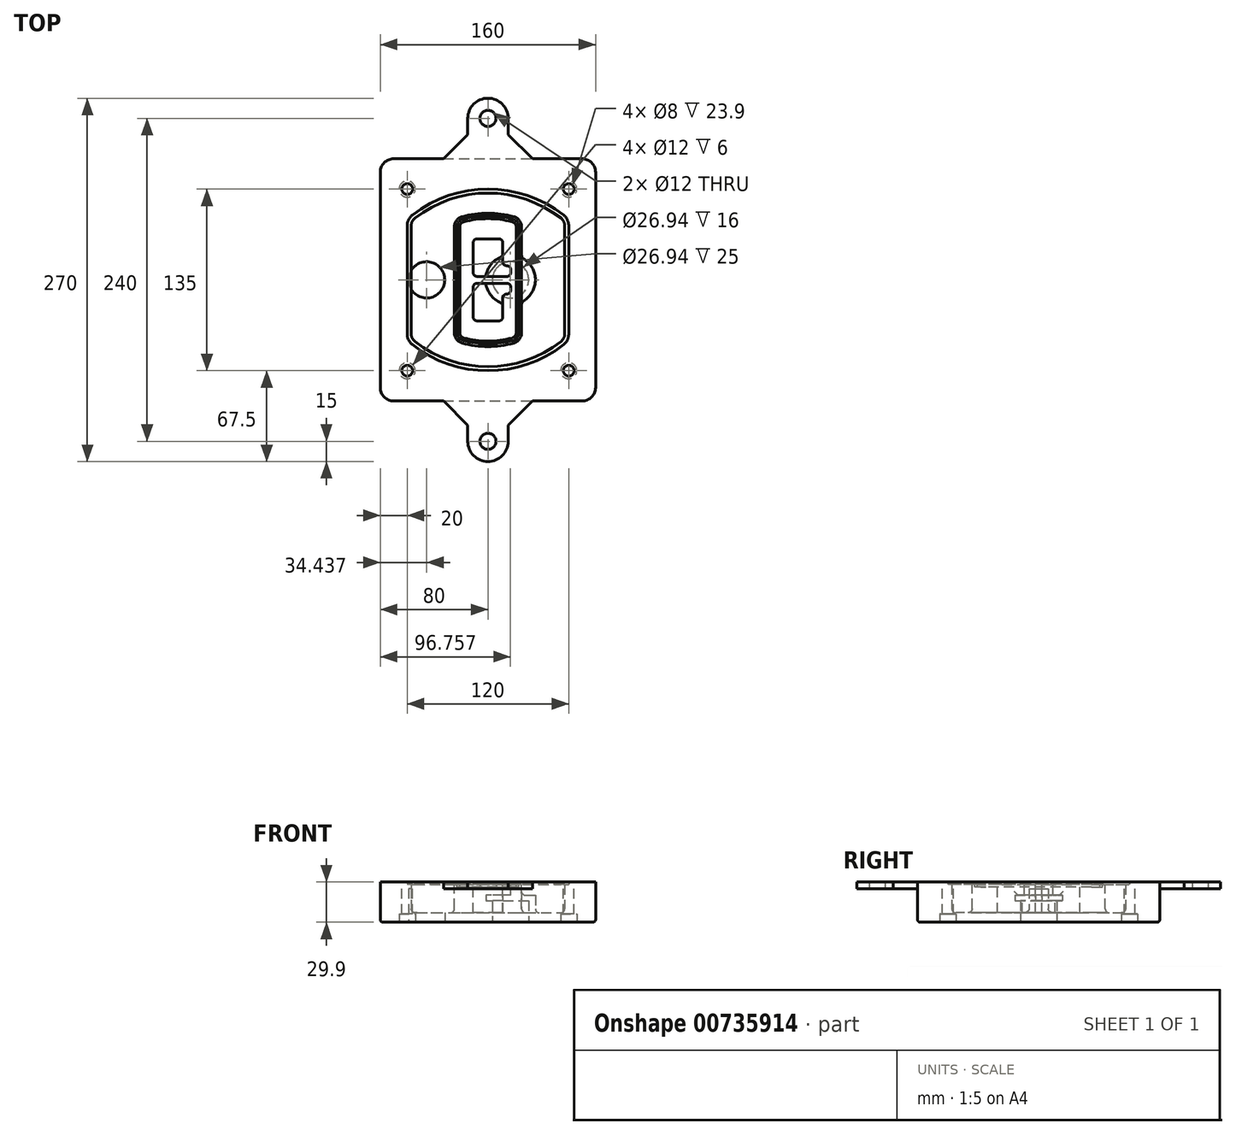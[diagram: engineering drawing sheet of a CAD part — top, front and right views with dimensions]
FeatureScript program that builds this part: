
annotation { "Feature Type Name" : "Feature", "Feature Type Description" : "" }
export const myFeature = defineFeature(function(context is Context, id is Id, definition is map)
    precondition{}
    {
        {
            var Q0;
            Q0=qCreatedBy(makeId("Top.planeOp"),FACE);
            var sketch = newSketch(context, id + "F0", { "sketchPlane" : qUnion([Q0])});
            skPoint(sketch, "E0.rect.middle", {"position": v(0, 0) * mm});
            skLineSegment(sketch, "E1.bottom", {"start": v(-70, -90) * mm, "end": v(70, -90) * mm});
            skLineSegment(sketch, "E1.top", {"start": v(-70, 90) * mm, "end": v(70, 90) * mm});
            skLineSegment(sketch, "E1.left", {"start": v(-80, -80) * mm, "end": v(-80, 80) * mm});
            skLineSegment(sketch, "E1.right", {"start": v(80, -80) * mm, "end": v(80, 80) * mm});
            skLineSegment(sketch, "E2", {"start": v(-80, 90) * mm, "end": v(80, -90) * mm, "construction": true});
            skLineSegment(sketch, "E3", {"start": v(80, 90) * mm, "end": v(-80, -90) * mm, "construction": true});
            skCircle(sketch, "E4", {"center": v(-60, 67.5) * mm, "radius": 4 * mm});
            skCircle(sketch, "E5", {"center": v(60, 67.5) * mm, "radius": 4 * mm});
            skCircle(sketch, "E6", {"center": v(60, -67.5) * mm, "radius": 4 * mm});
            skCircle(sketch, "E7", {"center": v(-60, -67.5) * mm, "radius": 4 * mm});
            skLineSegment(sketch, "E8", {"start": v(-60, 67.5) * mm, "end": v(60, 67.5) * mm, "construction": true});
            skLineSegment(sketch, "E9", {"start": v(60, 67.5) * mm, "end": v(60, -67.5) * mm, "construction": true});
            skLineSegment(sketch, "E10", {"start": v(60, -67.5) * mm, "end": v(-60, -67.5) * mm, "construction": true});
            skLineSegment(sketch, "E11", {"start": v(-60, -67.5) * mm, "end": v(-60, 67.5) * mm, "construction": true});
            skLineSegment(sketch, "E12", {"start": v(-60, 40.3) * mm, "end": v(-60, -40.3) * mm});
            skLineSegment(sketch, "E13", {"start": v(60, 40.3) * mm, "end": v(60, -40.3) * mm});
            skArc(sketch, "E14", {"start": v(56.15, 48.18) * mm, "mid": v(0, 67.5) * mm, "end": v(-56.15, 48.18) * mm});
            skArc(sketch, "E15", {"start": v(-56.15, -48.18) * mm, "mid": v(0, -67.5) * mm, "end": v(56.15, -48.18) * mm});
            skLineSegment(sketch, "E16", {"start": v(-60, 0) * mm, "end": v(60, 0) * mm, "construction": true});
            skPoint(sketch, "E17.visualSharp", {"position": v(-60, -45) * mm});
            skArc(sketch, "E17.filletArc", {"start": v(-60, -40.3) * mm, "mid": v(-58.99, -44.68) * mm, "end": v(-56.15, -48.18) * mm});
            skPoint(sketch, "E18.visualSharp", {"position": v(-60, 45) * mm});
            skArc(sketch, "E18.filletArc", {"start": v(-56.15, 48.18) * mm, "mid": v(-58.99, 44.68) * mm, "end": v(-60, 40.3) * mm});
            skPoint(sketch, "E19.visualSharp", {"position": v(60, 45) * mm});
            skArc(sketch, "E19.filletArc", {"start": v(60, 40.3) * mm, "mid": v(58.99, 44.68) * mm, "end": v(56.15, 48.18) * mm});
            skPoint(sketch, "E20.visualSharp", {"position": v(60, -45) * mm});
            skArc(sketch, "E20.filletArc", {"start": v(56.15, -48.18) * mm, "mid": v(58.99, -44.68) * mm, "end": v(60, -40.3) * mm});
            skPoint(sketch, "E21.visualSharp", {"position": v(-80, 90) * mm});
            skArc(sketch, "E21.filletArc", {"start": v(-70, 90) * mm, "mid": v(-77.07, 87.07) * mm, "end": v(-80, 80) * mm});
            skPoint(sketch, "E22.visualSharp", {"position": v(80, 90) * mm});
            skArc(sketch, "E22.filletArc", {"start": v(80, 80) * mm, "mid": v(77.07, 87.07) * mm, "end": v(70, 90) * mm});
            skPoint(sketch, "E23.visualSharp", {"position": v(80, -90) * mm});
            skArc(sketch, "E23.filletArc", {"start": v(70, -90) * mm, "mid": v(77.07, -87.07) * mm, "end": v(80, -80) * mm});
            skPoint(sketch, "E24.visualSharp", {"position": v(-80, -90) * mm});
            skArc(sketch, "E24.filletArc", {"start": v(-80, -80) * mm, "mid": v(-77.07, -87.07) * mm, "end": v(-70, -90) * mm});
            skArc(sketch, "E25.0", {"start": v(57, 40.3) * mm, "mid": v(56.3, 43.36) * mm, "end": v(54.3, 45.81) * mm});
            skLineSegment(sketch, "E25.1", {"start": v(57, 40.3) * mm, "end": v(57, -40.3) * mm});
            skArc(sketch, "E25.2", {"start": v(54.3, -45.81) * mm, "mid": v(56.3, -43.36) * mm, "end": v(57, -40.3) * mm});
            skArc(sketch, "E25.3", {"start": v(-54.3, -45.81) * mm, "mid": v(0, -64.5) * mm, "end": v(54.3, -45.81) * mm});
            skArc(sketch, "E25.4", {"start": v(-57, -40.3) * mm, "mid": v(-56.3, -43.36) * mm, "end": v(-54.3, -45.81) * mm});
            skArc(sketch, "E25.5", {"start": v(54.3, 45.81) * mm, "mid": v(0, 64.5) * mm, "end": v(-54.3, 45.81) * mm});
            skLineSegment(sketch, "E25.6", {"start": v(-57, 40.3) * mm, "end": v(-57, -40.3) * mm});
            skArc(sketch, "E25.7", {"start": v(-54.3, 45.81) * mm, "mid": v(-56.3, 43.36) * mm, "end": v(-57, 40.3) * mm});
            skArc(sketch, "E26.0", {"start": v(-58.62, 51.33) * mm, "mid": v(-62.58, 46.43) * mm, "end": v(-64, 40.3) * mm});
            skArc(sketch, "E26.1", {"start": v(58.62, 51.33) * mm, "mid": v(0, 71.5) * mm, "end": v(-58.62, 51.33) * mm});
            skArc(sketch, "E26.2", {"start": v(64, 40.3) * mm, "mid": v(62.58, 46.43) * mm, "end": v(58.62, 51.33) * mm});
            skLineSegment(sketch, "E26.3", {"start": v(64, 40.3) * mm, "end": v(64, -40.3) * mm});
            skArc(sketch, "E26.4", {"start": v(58.62, -51.33) * mm, "mid": v(62.58, -46.43) * mm, "end": v(64, -40.3) * mm});
            skLineSegment(sketch, "E26.5", {"start": v(-64, 40.3) * mm, "end": v(-64, -40.3) * mm});
            skArc(sketch, "E26.6", {"start": v(-58.62, -51.33) * mm, "mid": v(0, -71.5) * mm, "end": v(58.62, -51.33) * mm});
            skArc(sketch, "E26.7", {"start": v(-64, -40.3) * mm, "mid": v(-62.58, -46.43) * mm, "end": v(-58.62, -51.33) * mm});
            skSolve(sketch);
        }
        {
            var Q0;
            Q0=makeQuery(id+"F0.imprint","IMPRINT",FACE,{"disambiguationData":[TD([[makeQuery(id+"F0.imprint","IMPRINT",EDGE,{"derivedFrom":sQuery(id+"F0.wireOp",EDGE,"E1.bottom")}),1.0]])]});
            var Q1;
            Q1=makeQuery(id+"F0.imprint","IMPRINT",FACE,{"disambiguationData":[TD([[makeQuery(id+"F0.imprint","IMPRINT",EDGE,{"derivedFrom":sQuery(id+"F0.wireOp",EDGE,"E12")}),1.0]])]});
            var Q2;
            Q2=makeQuery(id+"F0.imprint","IMPRINT",FACE,{"disambiguationData":[TD([[makeQuery(id+"F0.imprint","IMPRINT",EDGE,{"derivedFrom":sQuery(id+"F0.wireOp",EDGE,"E25.0")}),1.0]])]});
            var Q3;
            Q3=makeQuery(id+"F0.imprint","IMPRINT",FACE,{"disambiguationData":[TD([[makeQuery(id+"F0.imprint","IMPRINT",EDGE,{"derivedFrom":sQuery(id+"F0.wireOp",EDGE,"E12")}),-1.0]])]});
            extrude(context, id + "F1", {"entities" : qUnion([Q0, Q1, Q2, Q3]), "oppositeDirection" : true, "depth" : 25 * mm});
        }
        {
            var Q0;
            Q0=makeQuery(id+"F0.imprint","IMPRINT",FACE,{"disambiguationData":[TD([[makeQuery(id+"F0.imprint","IMPRINT",EDGE,{"derivedFrom":sQuery(id+"F0.wireOp",EDGE,"E12")}),1.0]])]});
            extrude(context, id + "F2", {"entities" : qUnion([Q0]), "operationType" : NewBodyOperationType.ADD, "depth" : 3 * mm});
        }
        {
            var Q0;
            Q0=makeQuery(id+"F0.imprint","IMPRINT",FACE,{"disambiguationData":[TD([[makeQuery(id+"F0.imprint","IMPRINT",EDGE,{"derivedFrom":sQuery(id+"F0.wireOp",EDGE,"E25.0")}),1.0]])]});
            extrude(context, id + "F3", {"entities" : qUnion([Q0]), "operationType" : NewBodyOperationType.REMOVE, "oppositeDirection" : true, "depth" : 18 * mm});
        }
        {
            var Q0;
            Q0=makeQuery(id+"F2.opExtrude","CAP_FACE",FACE,{"disambiguationData":[OSD([sQuery(id+"F0.wireOp",EDGE,"E12"),sQuery(id+"F0.wireOp",EDGE,"E13"),sQuery(id+"F0.wireOp",EDGE,"E14"),sQuery(id+"F0.wireOp",EDGE,"E15"),sQuery(id+"F0.wireOp",EDGE,"E17.filletArc"),sQuery(id+"F0.wireOp",EDGE,"E18.filletArc"),sQuery(id+"F0.wireOp",EDGE,"E19.filletArc"),sQuery(id+"F0.wireOp",EDGE,"E20.filletArc"),sQuery(id+"F0.wireOp",EDGE,"E25.0"),sQuery(id+"F0.wireOp",EDGE,"E25.1"),sQuery(id+"F0.wireOp",EDGE,"E25.2"),sQuery(id+"F0.wireOp",EDGE,"E25.3"),sQuery(id+"F0.wireOp",EDGE,"E25.4"),sQuery(id+"F0.wireOp",EDGE,"E25.5"),sQuery(id+"F0.wireOp",EDGE,"E25.6"),sQuery(id+"F0.wireOp",EDGE,"E25.7")])],"isStart":false});
            var sketch = newSketch(context, id + "F4", { "sketchPlane" : qUnion([Q0])});
            skArc(sketch, "E27.0", {"start": v(-19.08, -46.97) * mm, "mid": v(0, -49.5) * mm, "end": v(19.08, -46.97) * mm});
            skArc(sketch, "E28.0", {"start": v(19.08, 46.97) * mm, "mid": v(0, 49.5) * mm, "end": v(-19.08, 46.97) * mm});
            skLineSegment(sketch, "E29", {"start": v(-25, 39.25) * mm, "end": v(-25, -39.25) * mm});
            skLineSegment(sketch, "E30", {"start": v(25, 39.25) * mm, "end": v(25, -39.25) * mm});
            skLineSegment(sketch, "E31", {"start": v(-25, 45.1) * mm, "end": v(25, 45.1) * mm, "construction": true});
            skLineSegment(sketch, "E32", {"start": v(-25, -45.1) * mm, "end": v(25, -45.1) * mm, "construction": true});
            skPoint(sketch, "E33.visualSharp", {"position": v(-25, 45.1) * mm});
            skArc(sketch, "E33.filletArc", {"start": v(-19.08, 46.97) * mm, "mid": v(-23.35, 44.11) * mm, "end": v(-25, 39.25) * mm});
            skPoint(sketch, "E34.visualSharp", {"position": v(25, 45.1) * mm});
            skArc(sketch, "E34.filletArc", {"start": v(25, 39.25) * mm, "mid": v(23.35, 44.11) * mm, "end": v(19.08, 46.97) * mm});
            skPoint(sketch, "E35.visualSharp", {"position": v(25, -45.1) * mm});
            skArc(sketch, "E35.filletArc", {"start": v(19.08, -46.97) * mm, "mid": v(23.35, -44.11) * mm, "end": v(25, -39.25) * mm});
            skPoint(sketch, "E36.visualSharp", {"position": v(-25, -45.1) * mm});
            skArc(sketch, "E36.filletArc", {"start": v(-25, -39.25) * mm, "mid": v(-23.35, -44.11) * mm, "end": v(-19.08, -46.97) * mm});
            skArc(sketch, "E37.0", {"start": v(54.3, 45.81) * mm, "mid": v(0, 64.5) * mm, "end": v(-54.3, 45.81) * mm});
            skArc(sketch, "E37.1", {"start": v(-54.3, 45.81) * mm, "mid": v(-56.3, 43.36) * mm, "end": v(-57, 40.3) * mm});
            skLineSegment(sketch, "E37.2", {"start": v(-57, 40.3) * mm, "end": v(-57, -40.3) * mm});
            skArc(sketch, "E37.3", {"start": v(-57, -40.3) * mm, "mid": v(-56.3, -43.36) * mm, "end": v(-54.3, -45.81) * mm});
            skArc(sketch, "E37.4", {"start": v(-54.3, -45.81) * mm, "mid": v(0, -64.5) * mm, "end": v(54.3, -45.81) * mm});
            skArc(sketch, "E37.5", {"start": v(54.3, -45.81) * mm, "mid": v(56.3, -43.36) * mm, "end": v(57, -40.3) * mm});
            skLineSegment(sketch, "E37.6", {"start": v(57, 40.3) * mm, "end": v(57, -40.3) * mm});
            skArc(sketch, "E37.7", {"start": v(57, 40.3) * mm, "mid": v(56.3, 43.36) * mm, "end": v(54.3, 45.81) * mm});
            skLineSegment(sketch, "E38.0", {"start": v(23, 39.25) * mm, "end": v(23, -39.25) * mm});
            skArc(sketch, "E38.1", {"start": v(18.56, -45.04) * mm, "mid": v(21.76, -42.9) * mm, "end": v(23, -39.25) * mm});
            skArc(sketch, "E38.2", {"start": v(-18.56, -45.04) * mm, "mid": v(0, -47.5) * mm, "end": v(18.56, -45.04) * mm});
            skArc(sketch, "E38.3", {"start": v(-23, -39.25) * mm, "mid": v(-21.76, -42.9) * mm, "end": v(-18.56, -45.04) * mm});
            skLineSegment(sketch, "E38.4", {"start": v(-23, 39.25) * mm, "end": v(-23, -39.25) * mm});
            skArc(sketch, "E38.5", {"start": v(23, 39.25) * mm, "mid": v(21.76, 42.9) * mm, "end": v(18.56, 45.04) * mm});
            skArc(sketch, "E38.6", {"start": v(-18.56, 45.04) * mm, "mid": v(-21.76, 42.9) * mm, "end": v(-23, 39.25) * mm});
            skArc(sketch, "E38.7", {"start": v(18.56, 45.04) * mm, "mid": v(0, 47.5) * mm, "end": v(-18.56, 45.04) * mm});
            skArc(sketch, "E39.0", {"start": v(21, 39.25) * mm, "mid": v(20.18, 41.68) * mm, "end": v(18.04, 43.1) * mm});
            skLineSegment(sketch, "E39.1", {"start": v(21, 39.25) * mm, "end": v(21, -39.25) * mm});
            skArc(sketch, "E39.2", {"start": v(18.04, -43.1) * mm, "mid": v(20.18, -41.68) * mm, "end": v(21, -39.25) * mm});
            skArc(sketch, "E39.3", {"start": v(-18.04, -43.1) * mm, "mid": v(0, -45.5) * mm, "end": v(18.04, -43.1) * mm});
            skArc(sketch, "E39.4", {"start": v(-21, -39.25) * mm, "mid": v(-20.18, -41.68) * mm, "end": v(-18.04, -43.1) * mm});
            skArc(sketch, "E39.5", {"start": v(18.04, 43.1) * mm, "mid": v(0, 45.5) * mm, "end": v(-18.04, 43.1) * mm});
            skLineSegment(sketch, "E39.6", {"start": v(-21, 39.25) * mm, "end": v(-21, -39.25) * mm});
            skArc(sketch, "E39.7", {"start": v(-18.04, 43.1) * mm, "mid": v(-20.18, 41.68) * mm, "end": v(-21, 39.25) * mm});
            skLineSegment(sketch, "E40", {"start": v(-25, 0) * mm, "end": v(25, 0) * mm, "construction": true});
            skLineSegment(sketch, "E41", {"start": v(-11, 5.5) * mm, "end": v(-11, 27.5) * mm});
            skLineSegment(sketch, "E42", {"start": v(-8, 30.5) * mm, "end": v(8, 30.5) * mm});
            skLineSegment(sketch, "E43", {"start": v(11, 27.5) * mm, "end": v(11, 13.5) * mm});
            skLineSegment(sketch, "E44", {"start": v(14, 10.5) * mm, "end": v(14, 10.5) * mm});
            skLineSegment(sketch, "E45", {"start": v(17, 7.5) * mm, "end": v(17, 5.5) * mm});
            skLineSegment(sketch, "E46", {"start": v(14, 2.5) * mm, "end": v(-8, 2.5) * mm});
            skPoint(sketch, "E47.visualSharp", {"position": v(-11, 30.5) * mm});
            skArc(sketch, "E47.filletArc", {"start": v(-8, 30.5) * mm, "mid": v(-10.12, 29.62) * mm, "end": v(-11, 27.5) * mm});
            skPoint(sketch, "E48.visualSharp", {"position": v(11, 30.5) * mm});
            skArc(sketch, "E48.filletArc", {"start": v(11, 27.5) * mm, "mid": v(10.12, 29.62) * mm, "end": v(8, 30.5) * mm});
            skPoint(sketch, "E49.visualSharp", {"position": v(11, 10.5) * mm});
            skArc(sketch, "E49.filletArc", {"start": v(11, 13.5) * mm, "mid": v(11.88, 11.38) * mm, "end": v(14, 10.5) * mm});
            skPoint(sketch, "E50.visualSharp", {"position": v(17, 10.5) * mm});
            skArc(sketch, "E50.filletArc", {"start": v(17, 7.5) * mm, "mid": v(16.12, 9.62) * mm, "end": v(14, 10.5) * mm});
            skPoint(sketch, "E51.visualSharp", {"position": v(17, 2.5) * mm});
            skArc(sketch, "E51.filletArc", {"start": v(14, 2.5) * mm, "mid": v(16.12, 3.38) * mm, "end": v(17, 5.5) * mm});
            skPoint(sketch, "E52.visualSharp", {"position": v(-11, 2.5) * mm});
            skArc(sketch, "E52.filletArc", {"start": v(-11, 5.5) * mm, "mid": v(-10.12, 3.38) * mm, "end": v(-8, 2.5) * mm});
            skLineSegment(sketch, "E53.0.MirrorCS", {"start": v(14, -2.5) * mm, "end": v(-8, -2.5) * mm});
            skArc(sketch, "E54.0.MirrorCS", {"start": v(-11, -5.5) * mm, "mid": v(-10.12, -3.38) * mm, "end": v(-8, -2.5) * mm});
            skLineSegment(sketch, "E55.0.MirrorCS", {"start": v(-11, -5.5) * mm, "end": v(-11, -27.5) * mm});
            skArc(sketch, "E56.0.MirrorCS", {"start": v(-8, -30.5) * mm, "mid": v(-10.12, -29.62) * mm, "end": v(-11, -27.5) * mm});
            skLineSegment(sketch, "E57.0.MirrorCS", {"start": v(-8, -30.5) * mm, "end": v(8, -30.5) * mm});
            skArc(sketch, "E58.0.MirrorCS", {"start": v(11, -27.5) * mm, "mid": v(10.12, -29.62) * mm, "end": v(8, -30.5) * mm});
            skLineSegment(sketch, "E59.0.MirrorCS", {"start": v(11, -27.5) * mm, "end": v(11, -13.5) * mm});
            skArc(sketch, "E60.0.MirrorCS", {"start": v(11, -13.5) * mm, "mid": v(11.88, -11.38) * mm, "end": v(14, -10.5) * mm});
            skArc(sketch, "E61.0.MirrorCS", {"start": v(17, -7.5) * mm, "mid": v(16.12, -9.62) * mm, "end": v(14, -10.5) * mm});
            skLineSegment(sketch, "E62.0.MirrorCS", {"start": v(17, -7.5) * mm, "end": v(17, -5.5) * mm});
            skArc(sketch, "E63.0.MirrorCS", {"start": v(14, -2.5) * mm, "mid": v(16.12, -3.38) * mm, "end": v(17, -5.5) * mm});
            skSolve(sketch);
        }
        {
            var Q0;
            Q0=makeQuery(id+"F4.imprint","IMPRINT",FACE,{"disambiguationData":[TD([[makeQuery(id+"F4.imprint","IMPRINT",EDGE,{"derivedFrom":sQuery(id+"F4.wireOp",EDGE,"E27.0")}),1.0]])]});
            var Q1;
            Q1=makeQuery(id+"F4.imprint","IMPRINT",FACE,{"disambiguationData":[TD([[makeQuery(id+"F4.imprint","IMPRINT",EDGE,{"derivedFrom":sQuery(id+"F4.wireOp",EDGE,"E38.0")}),-1.0]])]});
            var Q2;
            Q2=makeQuery(id+"F4.imprint","IMPRINT",FACE,{"disambiguationData":[TD([[makeQuery(id+"F4.imprint","IMPRINT",EDGE,{"derivedFrom":sQuery(id+"F4.wireOp",EDGE,"E39.0")}),1.0]])]});
            extrude(context, id + "F5", {"entities" : qUnion([Q0, Q1, Q2]), "operationType" : NewBodyOperationType.ADD, "endBound" : BoundingType.UP_TO_NEXT, "oppositeDirection" : true, "depth" : 25 * mm});
        }
        {
            var Q0;
            Q0=makeQuery(id+"F4.imprint","IMPRINT",FACE,{"disambiguationData":[TD([[makeQuery(id+"F4.imprint","IMPRINT",EDGE,{"derivedFrom":sQuery(id+"F4.wireOp",EDGE,"E38.0")}),-1.0]])]});
            extrude(context, id + "F6", {"entities" : qUnion([Q0]), "operationType" : NewBodyOperationType.REMOVE, "oppositeDirection" : true, "depth" : 2 * mm});
        }
        {
            var Q0;
            Q0=makeQuery(id+"F1.opExtrude","CAP_FACE",FACE,{"disambiguationData":[OSD([sQuery(id+"F0.wireOp",EDGE,"E1.bottom"),sQuery(id+"F0.wireOp",EDGE,"E1.top"),sQuery(id+"F0.wireOp",EDGE,"E1.left"),sQuery(id+"F0.wireOp",EDGE,"E1.right"),sQuery(id+"F0.wireOp",EDGE,"E4"),sQuery(id+"F0.wireOp",EDGE,"E5"),sQuery(id+"F0.wireOp",EDGE,"E6"),sQuery(id+"F0.wireOp",EDGE,"E7"),sQuery(id+"F0.wireOp",EDGE,"E21.filletArc"),sQuery(id+"F0.wireOp",EDGE,"E22.filletArc"),sQuery(id+"F0.wireOp",EDGE,"E23.filletArc"),sQuery(id+"F0.wireOp",EDGE,"E24.filletArc")])],"isStart":false});
            var sketch = newSketch(context, id + "F7", { "sketchPlane" : qUnion([Q0])});
            skCircle(sketch, "E64", {"center": v(16.76, 0) * mm, "radius": 13.47 * mm});
            skCircle(sketch, "E65", {"center": v(-45.56, 0) * mm, "radius": 13.47 * mm});
            skLineSegment(sketch, "E66", {"start": v(80, 0) * mm, "end": v(-80, 0) * mm});
            skCircle(sketch, "E67", {"center": v(16.76, 0) * mm, "radius": 18.47 * mm});
            skCircle(sketch, "E68", {"center": v(60, -67.5) * mm, "radius": 6 * mm});
            skCircle(sketch, "E69", {"center": v(-60, -67.5) * mm, "radius": 6 * mm});
            skCircle(sketch, "E70", {"center": v(-60, 67.5) * mm, "radius": 6 * mm});
            skCircle(sketch, "E71", {"center": v(60, 67.5) * mm, "radius": 6 * mm});
            skSolve(sketch);
        }
        {
            var Q0;
            {var subQ1=sQuery(id+"F7.wireOp",EDGE,"E66");var subQ4=sQuery(id+"F7.wireOp",EDGE,"E64");var subQ6=makeQuery(id+"F7.imprint","INTERSECT",VERTEX,{"disambiguationData":[OD(0.0)],"derivedFrom":[subQ4,subQ1]});Q0=makeQuery(id+"F7.imprint","IMPRINT",FACE,{"disambiguationData":[TD([[makeQuery(id+"F7.imprint","IMPRINT",EDGE,{"disambiguationData":[TD([[subQ6,-1.0]])],"derivedFrom":subQ4}),-1.0]])]});}
            var Q1;
            {var subQ0=sQuery(id+"F7.wireOp",EDGE,"E66");var subQ1=sQuery(id+"F7.wireOp",EDGE,"E64");var subQ3=makeQuery(id+"F7.imprint","INTERSECT",VERTEX,{"disambiguationData":[OD(0.0)],"derivedFrom":[subQ1,subQ0]});Q1=makeQuery(id+"F7.imprint","IMPRINT",FACE,{"disambiguationData":[TD([[makeQuery(id+"F7.imprint","IMPRINT",EDGE,{"disambiguationData":[TD([[subQ3,-1.0]])],"derivedFrom":subQ1}),1.0]])]});}
            var Q2;
            {var subQ0=sQuery(id+"F7.wireOp",EDGE,"E66");var subQ1=sQuery(id+"F7.wireOp",EDGE,"E64");var subQ3=makeQuery(id+"F7.imprint","INTERSECT",VERTEX,{"disambiguationData":[OD(0.0)],"derivedFrom":[subQ1,subQ0]});Q2=makeQuery(id+"F7.imprint","IMPRINT",FACE,{"disambiguationData":[TD([[makeQuery(id+"F7.imprint","IMPRINT",EDGE,{"disambiguationData":[TD([[subQ3,1.0]])],"derivedFrom":subQ1}),1.0]])]});}
            var Q3;
            {var subQ1=sQuery(id+"F7.wireOp",EDGE,"E66");var subQ4=sQuery(id+"F7.wireOp",EDGE,"E64");var subQ6=makeQuery(id+"F7.imprint","INTERSECT",VERTEX,{"disambiguationData":[OD(0.0)],"derivedFrom":[subQ4,subQ1]});Q3=makeQuery(id+"F7.imprint","IMPRINT",FACE,{"disambiguationData":[TD([[makeQuery(id+"F7.imprint","IMPRINT",EDGE,{"disambiguationData":[TD([[subQ6,1.0]])],"derivedFrom":subQ4}),-1.0]])]});}
            extrude(context, id + "F8", {"entities" : qUnion([Q0, Q1, Q2, Q3]), "operationType" : NewBodyOperationType.ADD, "oppositeDirection" : true, "depth" : 20 * mm});
        }
        {
            var Q0;
            {var subQ0=sQuery(id+"F7.wireOp",EDGE,"E66");var subQ1=sQuery(id+"F7.wireOp",EDGE,"E64");var subQ3=makeQuery(id+"F7.imprint","INTERSECT",VERTEX,{"disambiguationData":[OD(0.0)],"derivedFrom":[subQ1,subQ0]});Q0=makeQuery(id+"F7.imprint","IMPRINT",FACE,{"disambiguationData":[TD([[makeQuery(id+"F7.imprint","IMPRINT",EDGE,{"disambiguationData":[TD([[subQ3,-1.0]])],"derivedFrom":subQ1}),1.0]])]});}
            var Q1;
            {var subQ0=sQuery(id+"F7.wireOp",EDGE,"E66");var subQ1=sQuery(id+"F7.wireOp",EDGE,"E64");var subQ3=makeQuery(id+"F7.imprint","INTERSECT",VERTEX,{"disambiguationData":[OD(0.0)],"derivedFrom":[subQ1,subQ0]});Q1=makeQuery(id+"F7.imprint","IMPRINT",FACE,{"disambiguationData":[TD([[makeQuery(id+"F7.imprint","IMPRINT",EDGE,{"disambiguationData":[TD([[subQ3,1.0]])],"derivedFrom":subQ1}),1.0]])]});}
            extrude(context, id + "F9", {"entities" : qUnion([Q0, Q1]), "operationType" : NewBodyOperationType.REMOVE, "oppositeDirection" : true, "depth" : 16 * mm});
        }
        {
            var Q0;
            {var subQ0=sQuery(id+"F7.wireOp",EDGE,"E66");var subQ1=sQuery(id+"F7.wireOp",EDGE,"E65");var subQ3=makeQuery(id+"F7.imprint","INTERSECT",VERTEX,{"disambiguationData":[OD(0.0)],"derivedFrom":[subQ1,subQ0]});Q0=makeQuery(id+"F7.imprint","IMPRINT",FACE,{"disambiguationData":[TD([[makeQuery(id+"F7.imprint","IMPRINT",EDGE,{"disambiguationData":[TD([[subQ3,-1.0]])],"derivedFrom":subQ1}),1.0]])]});}
            var Q1;
            {var subQ0=sQuery(id+"F7.wireOp",EDGE,"E66");var subQ1=sQuery(id+"F7.wireOp",EDGE,"E65");var subQ3=makeQuery(id+"F7.imprint","INTERSECT",VERTEX,{"disambiguationData":[OD(0.0)],"derivedFrom":[subQ1,subQ0]});Q1=makeQuery(id+"F7.imprint","IMPRINT",FACE,{"disambiguationData":[TD([[makeQuery(id+"F7.imprint","IMPRINT",EDGE,{"disambiguationData":[TD([[subQ3,1.0]])],"derivedFrom":subQ1}),1.0]])]});}
            extrude(context, id + "F10", {"entities" : qUnion([Q0, Q1]), "operationType" : NewBodyOperationType.REMOVE, "oppositeDirection" : true, "depth" : 25 * mm});
        }
        {
            var Q0;
            Q0=makeQuery(id+"F7.imprint","IMPRINT",FACE,{"disambiguationData":[TD([[makeQuery(id+"F7.imprint","IMPRINT",EDGE,{"derivedFrom":sQuery(id+"F7.wireOp",EDGE,"E68")}),1.0]])]});
            var Q1;
            Q1=makeQuery(id+"F7.imprint","IMPRINT",FACE,{"disambiguationData":[TD([[makeQuery(id+"F7.imprint","IMPRINT",EDGE,{"derivedFrom":makeQuery(id+"F1.opExtrude","CAP_EDGE",EDGE,{"disambiguationData":[OSD([sQuery(id+"F0.wireOp",EDGE,"E5")])],"isStart":false})}),-1.0]])]});
            var Q2;
            Q2=makeQuery(id+"F7.imprint","IMPRINT",FACE,{"disambiguationData":[TD([[makeQuery(id+"F7.imprint","IMPRINT",EDGE,{"derivedFrom":sQuery(id+"F7.wireOp",EDGE,"E69")}),1.0]])]});
            var Q3;
            Q3=makeQuery(id+"F7.imprint","IMPRINT",FACE,{"disambiguationData":[TD([[makeQuery(id+"F7.imprint","IMPRINT",EDGE,{"derivedFrom":makeQuery(id+"F1.opExtrude","CAP_EDGE",EDGE,{"disambiguationData":[OSD([sQuery(id+"F0.wireOp",EDGE,"E4")])],"isStart":false})}),-1.0]])]});
            var Q4;
            Q4=makeQuery(id+"F7.imprint","IMPRINT",FACE,{"disambiguationData":[TD([[makeQuery(id+"F7.imprint","IMPRINT",EDGE,{"derivedFrom":sQuery(id+"F7.wireOp",EDGE,"E70")}),1.0]])]});
            var Q5;
            Q5=makeQuery(id+"F7.imprint","IMPRINT",FACE,{"disambiguationData":[TD([[makeQuery(id+"F7.imprint","IMPRINT",EDGE,{"derivedFrom":makeQuery(id+"F1.opExtrude","CAP_EDGE",EDGE,{"disambiguationData":[OSD([sQuery(id+"F0.wireOp",EDGE,"E7")])],"isStart":false})}),-1.0]])]});
            var Q6;
            Q6=makeQuery(id+"F7.imprint","IMPRINT",FACE,{"disambiguationData":[TD([[makeQuery(id+"F7.imprint","IMPRINT",EDGE,{"derivedFrom":sQuery(id+"F7.wireOp",EDGE,"E71")}),1.0]])]});
            var Q7;
            Q7=makeQuery(id+"F7.imprint","IMPRINT",FACE,{"disambiguationData":[TD([[makeQuery(id+"F7.imprint","IMPRINT",EDGE,{"derivedFrom":makeQuery(id+"F1.opExtrude","CAP_EDGE",EDGE,{"disambiguationData":[OSD([sQuery(id+"F0.wireOp",EDGE,"E6")])],"isStart":false})}),-1.0]])]});
            extrude(context, id + "F11", {"entities" : qUnion([Q0, Q1, Q2, Q3, Q4, Q5, Q6, Q7]), "operationType" : NewBodyOperationType.REMOVE, "oppositeDirection" : true, "depth" : 6 * mm});
        }
        {
            var Q0;
            Q0=makeQuery(id+"F9.boolean.opBoolean","COPY",FACE,{"derivedFrom":makeQuery(id+"F9.opExtrude","CAP_FACE",FACE,{"disambiguationData":[OSD([sQuery(id+"F7.wireOp",EDGE,"E64")])],"isStart":false})});
            var sketch = newSketch(context, id + "F12", { "sketchPlane" : qUnion([Q0])});
            skArc(sketch, "E72.0", {"start": v(11, 17.55) * mm, "mid": v(2.57, 11.82) * mm, "end": v(-1.54, 2.5) * mm});
            skArc(sketch, "E72.1", {"start": v(-1.54, -2.5) * mm, "mid": v(2.57, -11.82) * mm, "end": v(11, -17.55) * mm});
            skLineSegment(sketch, "E73", {"start": v(-1.54, -2.5) * mm, "end": v(14, -2.5) * mm});
            skLineSegment(sketch, "E74.0", {"start": v(14, 2.5) * mm, "end": v(-1.54, 2.5) * mm});
            skArc(sketch, "E74.1", {"start": v(14, 2.5) * mm, "mid": v(16.12, 3.38) * mm, "end": v(17, 5.5) * mm});
            skLineSegment(sketch, "E74.2", {"start": v(17, 7.5) * mm, "end": v(17, 5.5) * mm});
            skArc(sketch, "E74.3", {"start": v(17, 7.5) * mm, "mid": v(16.12, 9.62) * mm, "end": v(14, 10.5) * mm});
            skArc(sketch, "E74.4", {"start": v(11, 13.5) * mm, "mid": v(11.88, 11.38) * mm, "end": v(14, 10.5) * mm});
            skLineSegment(sketch, "E74.5", {"start": v(11, 17.55) * mm, "end": v(11, 13.5) * mm});
            skLineSegment(sketch, "E74.7", {"start": v(14, -2.5) * mm, "end": v(-1.54, -2.5) * mm});
            skArc(sketch, "E74.8", {"start": v(14, -2.5) * mm, "mid": v(16.12, -3.38) * mm, "end": v(17, -5.5) * mm});
            skLineSegment(sketch, "E74.9", {"start": v(17, -7.5) * mm, "end": v(17, -5.5) * mm});
            skArc(sketch, "E74.10", {"start": v(17, -7.5) * mm, "mid": v(16.12, -9.62) * mm, "end": v(14, -10.5) * mm});
            skArc(sketch, "E74.11", {"start": v(11, -13.5) * mm, "mid": v(11.88, -11.38) * mm, "end": v(14, -10.5) * mm});
            skLineSegment(sketch, "E74.12", {"start": v(11, -17.55) * mm, "end": v(11, -13.5) * mm});
            skPoint(sketch, "E75.orphan", {"position": v(11, -27.5) * mm});
            skPoint(sketch, "E76.orphan", {"position": v(-8, -2.5) * mm});
            skPoint(sketch, "E77.orphan", {"position": v(-8, 2.5) * mm});
            skPoint(sketch, "E78.orphan", {"position": v(11, 27.5) * mm});
            skSolve(sketch);
        }
        {
            var Q0;
            {var subQ7=sQuery(id+"F12.wireOp",EDGE,"E72.0");var subQ14=sQuery(id+"F12.wireOp",EDGE,"E72.1");var subQ16=sQuery(id+"F12.wireOp",EDGE,"E74.1");var subQ18=sQuery(id+"F12.wireOp",EDGE,"E74.8");Q0=qUnion([makeQuery(id+"F12.imprint","IMPRINT",FACE,{"disambiguationData":[TD([[makeQuery(id+"F12.imprint","IMPRINT",EDGE,{"derivedFrom":subQ7}),1.0]])]}),makeQuery(id+"F12.imprint","IMPRINT",FACE,{"disambiguationData":[TD([[makeQuery(id+"F12.imprint","IMPRINT",EDGE,{"derivedFrom":subQ14}),1.0]])]}),makeQuery(id+"F12.imprint","IMPRINT",FACE,{"disambiguationData":[TD([[makeQuery(id+"F12.imprint","IMPRINT",EDGE,{"derivedFrom":subQ16}),1.0]])]}),makeQuery(id+"F12.imprint","IMPRINT",FACE,{"disambiguationData":[TD([[makeQuery(id+"F12.imprint","IMPRINT",EDGE,{"derivedFrom":subQ18}),-1.0]])]})]);}
            var Q1;
            Q1=makeQuery(id+"F5.boolean.opBoolean","SPLIT",FACE,{"disambiguationData":[TD([makeQuery(id+"F5.opExtrude","SWEPT_FACE",FACE,{"disambiguationData":[OSD([sQuery(id+"F4.wireOp",EDGE,"E41")])]})])],"derivedFrom":makeQuery(id+"F3.boolean.opBoolean","COPY",FACE,{"derivedFrom":makeQuery(id+"F3.opExtrude","CAP_FACE",FACE,{"disambiguationData":[OSD([sQuery(id+"F0.wireOp",EDGE,"E25.0"),sQuery(id+"F0.wireOp",EDGE,"E25.1"),sQuery(id+"F0.wireOp",EDGE,"E25.2"),sQuery(id+"F0.wireOp",EDGE,"E25.3"),sQuery(id+"F0.wireOp",EDGE,"E25.4"),sQuery(id+"F0.wireOp",EDGE,"E25.5"),sQuery(id+"F0.wireOp",EDGE,"E25.6"),sQuery(id+"F0.wireOp",EDGE,"E25.7")])],"isStart":false})})});
            extrude(context, id + "F13", {"entities" : qUnion([Q0]), "operationType" : NewBodyOperationType.REMOVE, "endBound" : BoundingType.UP_TO_SURFACE, "endBoundEntityFace" : qUnion([Q1]), "depth" : 25 * mm});
        }
        {
            var Q0;
            Q0=makeQuery(id+"F3.boolean.opBoolean","COPY",EDGE,{"derivedFrom":makeQuery(id+"F3.opExtrude","CAP_EDGE",EDGE,{"disambiguationData":[OSD([sQuery(id+"F0.wireOp",EDGE,"E25.6")])],"isStart":false})});
            var Q1;
            Q1=makeQuery(id+"F8.boolean.opBoolean","INTERSECT",EDGE,{"derivedFrom":[makeQuery(id+"F5.opExtrude","SWEPT_FACE",FACE,{"disambiguationData":[OSD([sQuery(id+"F4.wireOp",EDGE,"E30")])]}),makeQuery(id+"F8.opExtrude","CAP_FACE",FACE,{"disambiguationData":[OSD([sQuery(id+"F7.wireOp",EDGE,"E67")])],"isStart":false})]});
            var Q2;
            Q2=makeQuery(id+"F8.boolean.opBoolean","INTERSECT",EDGE,{"disambiguationData":[OD(1.0)],"derivedFrom":[makeQuery(id+"F5.opExtrude","SWEPT_FACE",FACE,{"disambiguationData":[OSD([sQuery(id+"F4.wireOp",EDGE,"E30")])]}),makeQuery(id+"F8.opExtrude","SWEPT_FACE",FACE,{"disambiguationData":[OSD([sQuery(id+"F7.wireOp",EDGE,"E67")])]})]});
            var Q3;
            {var subQ0=sQuery(id+"F4.wireOp",EDGE,"E30");Q3=makeQuery(id+"F8.boolean.opBoolean","SPLIT",EDGE,{"disambiguationData":[TD([makeQuery(id+"F5.opExtrude","SWEPT_FACE",FACE,{"disambiguationData":[OSD([sQuery(id+"F4.wireOp",EDGE,"E35.filletArc")])]})])],"derivedFrom":makeQuery(id+"F5.opExtrude","CAP_EDGE",EDGE,{"disambiguationData":[OSD([subQ0])],"isStart":false})});}
            var Q4;
            {var subQ0=sQuery(id+"F0.wireOp",EDGE,"E25.7");var subQ1=sQuery(id+"F0.wireOp",EDGE,"E25.1");var subQ2=sQuery(id+"F0.wireOp",EDGE,"E25.6");var subQ3=sQuery(id+"F0.wireOp",EDGE,"E25.5");var subQ4=sQuery(id+"F0.wireOp",EDGE,"E25.4");var subQ5=sQuery(id+"F0.wireOp",EDGE,"E25.0");var subQ6=sQuery(id+"F0.wireOp",EDGE,"E25.2");var subQ7=sQuery(id+"F0.wireOp",EDGE,"E25.3");Q4=makeQuery(id+"F8.boolean.opBoolean","INTERSECT",EDGE,{"derivedFrom":[makeQuery(id+"F5.boolean.opBoolean","SPLIT",FACE,{"disambiguationData":[TD([makeQuery(id+"F2.opExtrude","SWEPT_FACE",FACE,{"disambiguationData":[OSD([subQ5])]})])],"derivedFrom":makeQuery(id+"F3.boolean.opBoolean","COPY",FACE,{"derivedFrom":makeQuery(id+"F3.opExtrude","CAP_FACE",FACE,{"disambiguationData":[OSD([subQ5,subQ1,subQ6,subQ7,subQ4,subQ3,subQ2,subQ0])],"isStart":false})})}),makeQuery(id+"F8.opExtrude","SWEPT_FACE",FACE,{"disambiguationData":[OSD([sQuery(id+"F7.wireOp",EDGE,"E67")])]})]});}
            var Q5;
            Q5=makeQuery(id+"F8.boolean.opBoolean","INTERSECT",EDGE,{"disambiguationData":[OD(0.0)],"derivedFrom":[makeQuery(id+"F5.opExtrude","SWEPT_FACE",FACE,{"disambiguationData":[OSD([sQuery(id+"F4.wireOp",EDGE,"E30")])]}),makeQuery(id+"F8.opExtrude","SWEPT_FACE",FACE,{"disambiguationData":[OSD([sQuery(id+"F7.wireOp",EDGE,"E67")])]})]});
            fillet(context, id + "F14", {"entities" : qUnion([Q0, Q1, Q2, Q3, Q4, Q5]), "radius" : 3 * mm, "tangentPropagation" : true, "allowEdgeOverflow" : false});
        }
        {
            var Q0;
            Q0=makeQuery(id+"F1.opExtrude","CAP_EDGE",EDGE,{"disambiguationData":[OSD([sQuery(id+"F0.wireOp",EDGE,"E1.bottom")])],"isStart":false});
            fillet(context, id + "F15", {"entities" : qUnion([Q0]), "radius" : 2 * mm, "tangentPropagation" : true, "allowEdgeOverflow" : false});
        }
        {
            var Q0;
            {var subQ0=sQuery(id+"F0.wireOp",EDGE,"E21.filletArc");var subQ1=sQuery(id+"F0.wireOp",EDGE,"E7");var subQ2=sQuery(id+"F0.wireOp",EDGE,"E6");var subQ3=sQuery(id+"F0.wireOp",EDGE,"E5");var subQ4=sQuery(id+"F0.wireOp",EDGE,"E4");var subQ5=sQuery(id+"F0.wireOp",EDGE,"E22.filletArc");var subQ6=sQuery(id+"F0.wireOp",EDGE,"E1.bottom");var subQ7=sQuery(id+"F0.wireOp",EDGE,"E1.right");var subQ8=sQuery(id+"F0.wireOp",EDGE,"E1.top");var subQ9=sQuery(id+"F0.wireOp",EDGE,"E1.left");var subQ10=sQuery(id+"F0.wireOp",EDGE,"E23.filletArc");var subQ11=sQuery(id+"F0.wireOp",EDGE,"E24.filletArc");Q0=makeQuery(id+"F2.boolean.opBoolean","SPLIT",FACE,{"disambiguationData":[TD([makeQuery(id+"F1.opExtrude","SWEPT_FACE",FACE,{"disambiguationData":[OSD([subQ6])]})])],"derivedFrom":makeQuery(id+"F1.opExtrude","CAP_FACE",FACE,{"disambiguationData":[OSD([subQ6,subQ8,subQ9,subQ7,subQ4,subQ3,subQ2,subQ1,subQ0,subQ5,subQ10,subQ11])],"isStart":true})});}
            var sketch = newSketch(context, id + "F16", { "sketchPlane" : qUnion([Q0])});
            skLineSegment(sketch, "E79", {"start": v(0, 90) * mm, "end": v(0, 120) * mm, "construction": true});
            skCircle(sketch, "E80", {"center": v(0, 120) * mm, "radius": 6 * mm});
            skLineSegment(sketch, "E81", {"start": v(-15, 108) * mm, "end": v(-15, 120) * mm});
            skLineSegment(sketch, "E82", {"start": v(33, 90) * mm, "end": v(15, 108) * mm});
            skLineSegment(sketch, "E83", {"start": v(15, 108) * mm, "end": v(15, 120) * mm});
            skArc(sketch, "E84", {"start": v(15, 120) * mm, "mid": v(0, 135) * mm, "end": v(-15, 120) * mm});
            skLineSegment(sketch, "E85", {"start": v(33, 90) * mm, "end": v(32.84, 90) * mm});
            skLineSegment(sketch, "E86", {"start": v(-15, 108) * mm, "end": v(-33, 90) * mm});
            skLineSegment(sketch, "E87", {"start": v(80, 0) * mm, "end": v(-80, 0) * mm, "construction": true});
            skLineSegment(sketch, "E88.MirrorCS", {"start": v(-15, -108) * mm, "end": v(-33, -90) * mm});
            skLineSegment(sketch, "E89.MirrorCS", {"start": v(33, -90) * mm, "end": v(15, -108) * mm});
            skLineSegment(sketch, "E90.MirrorCS", {"start": v(33, -90) * mm, "end": v(32.84, -90) * mm});
            skLineSegment(sketch, "E91.MirrorCS", {"start": v(0, -90) * mm, "end": v(0, -120) * mm, "construction": true});
            skCircle(sketch, "E92.MirrorC", {"center": v(0, -120) * mm, "radius": 6 * mm});
            skArc(sketch, "E93.MirrorCS", {"start": v(15, -120) * mm, "mid": v(0, -135) * mm, "end": v(-15, -120) * mm});
            skLineSegment(sketch, "E94.MirrorCS", {"start": v(15, -108) * mm, "end": v(15, -120) * mm});
            skLineSegment(sketch, "E95.MirrorCS", {"start": v(-15, -108) * mm, "end": v(-15, -120) * mm});
            skSolve(sketch);
        }
        {
            var Q0;
            {var subQ0=sQuery(id+"F16.wireOp",EDGE,"E90.MirrorCS");Q0=makeQuery(id+"F16.imprint","IMPRINT",FACE,{"disambiguationData":[TD([[makeQuery(id+"F16.imprint","IMPRINT",EDGE,{"derivedFrom":subQ0}),-1.0]])]});}
            var Q1;
            {var subQ5=sQuery(id+"F16.wireOp",EDGE,"E85");Q1=makeQuery(id+"F16.imprint","IMPRINT",FACE,{"disambiguationData":[TD([[makeQuery(id+"F16.imprint","IMPRINT",EDGE,{"derivedFrom":subQ5}),-1.0]])]});}
            var Q2;
            Q2=makeQuery(id+"F16.imprint","IMPRINT",FACE,{"disambiguationData":[TD([[makeQuery(id+"F16.imprint","IMPRINT",EDGE,{"derivedFrom":sQuery(id+"F16.wireOp",EDGE,"E80")}),-1.0]])]});
            extrude(context, id + "F17", {"entities" : qUnion([Q0, Q1, Q2]), "operationType" : NewBodyOperationType.ADD, "depth" : 4.9 * mm, "offsetDistance" : 25 * mm});
        }
    });
